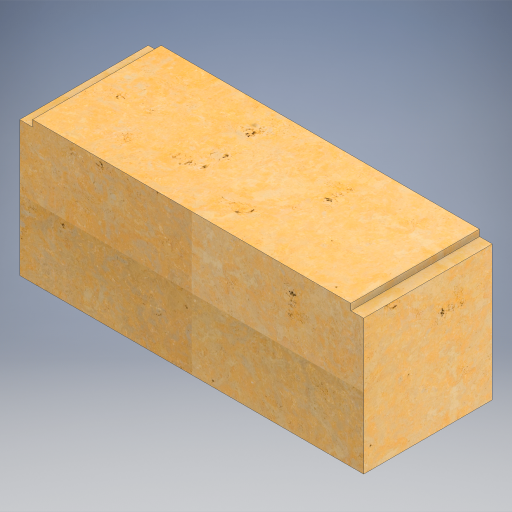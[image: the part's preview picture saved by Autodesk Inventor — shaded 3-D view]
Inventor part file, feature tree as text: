
AUTODESK INVENTOR PART (.ipt)
format: ipt  version: 2023 (Build 270158030, 158C)  size: 538,624 bytes
history: native  units: in
note: dims shown in document units (in); Inventor stores cm internally (conversion verified against a paired STEP export)
features: extrude x2, sketch x2
ambient origin geometry x8: Origin, YZ Plane, XZ Plane, XY Plane, X Axis, Y Axis, Z Axis, Center Point
bodies: Solid1 (feature_tree)
feature tree (4):
  extrude  "Extrusion1"  Depth=22.0in
  extrude  "Extrusion2"  Depth=2.0in
  sketch  "Sketch1"  dims[d0=53.5in d1=22.0in]
  sketch  "Sketch2"  dims[d2=1.0in d3=2.0in d4=1.0in d5=2.0in d6=20.0in d7=0.0in d8=1.0in d9=1.0in d10=9.0in d11=9.0in d12=3.25in d13=0.0in]
